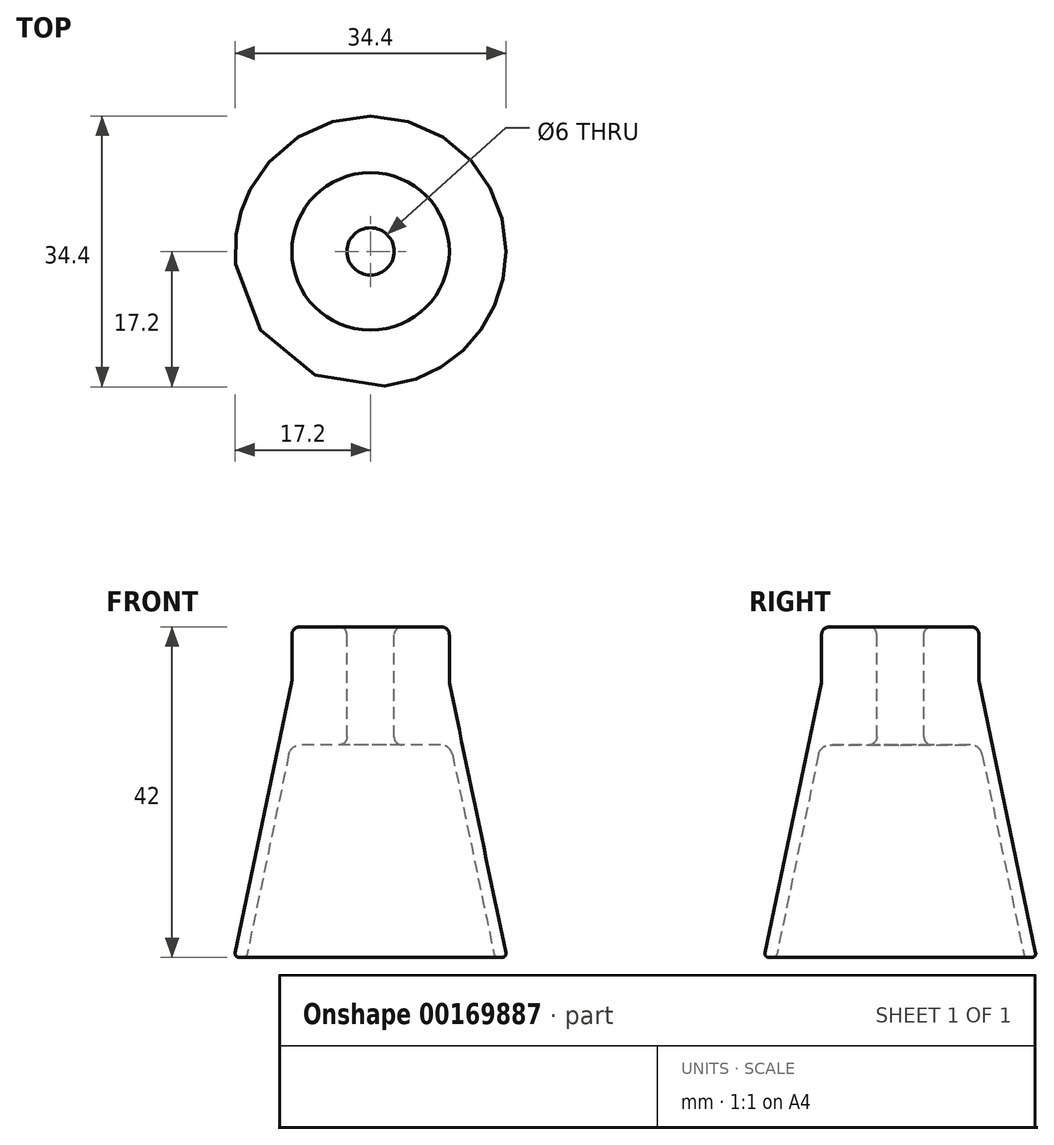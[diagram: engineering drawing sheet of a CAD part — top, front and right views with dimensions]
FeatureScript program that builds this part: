
annotation { "Feature Type Name" : "Feature", "Feature Type Description" : "" }
export const myFeature = defineFeature(function(context is Context, id is Id, definition is map)
    precondition{}
    {
        {
            var Q0;
            Q0=qCreatedBy(makeId("Right.planeOp"),FACE);
            var sketch = newSketch(context, id + "F0", { "sketchPlane" : qUnion([Q0])});
            skLineSegment(sketch, "E0", {"start": v(0, 42) * mm, "end": v(0, 0) * mm, "construction": true});
            skLineSegment(sketch, "E1", {"start": v(-4, 42) * mm, "end": v(-9, 42) * mm});
            skLineSegment(sketch, "E2", {"start": v(-10, 41) * mm, "end": v(-10, 35.16) * mm});
            skLineSegment(sketch, "E3", {"start": v(-10.03, 34.85) * mm, "end": v(-17.19, 0.6) * mm});
            skLineSegment(sketch, "E4", {"start": v(-16.7, 0) * mm, "end": v(-16.19, 0) * mm});
            skLineSegment(sketch, "E5", {"start": v(-15.7, 0.4) * mm, "end": v(-10.39, 25.8) * mm});
            skLineSegment(sketch, "E6", {"start": v(-8.92, 27) * mm, "end": v(-4, 27) * mm});
            skLineSegment(sketch, "E7", {"start": v(-3, 28) * mm, "end": v(-3, 41) * mm});
            skLineSegment(sketch, "E8", {"start": v(-10, 42) * mm, "end": v(0, 42) * mm, "construction": true});
            skLineSegment(sketch, "E9", {"start": v(0, 0) * mm, "end": v(-18, 0) * mm, "construction": true});
            skLineSegment(sketch, "E10", {"start": v(0, 35.16) * mm, "end": v(-3, 35.16) * mm, "construction": true});
            skPoint(sketch, "E11.visualSharp", {"position": v(-3, 27) * mm});
            skArc(sketch, "E11.filletArc", {"start": v(-4, 27) * mm, "mid": v(-3.3, 27.3) * mm, "end": v(-3, 28) * mm});
            skPoint(sketch, "E12.visualSharp", {"position": v(-3, 42) * mm});
            skArc(sketch, "E12.filletArc", {"start": v(-3, 41) * mm, "mid": v(-3.3, 41.7) * mm, "end": v(-4, 42) * mm});
            skPoint(sketch, "E13.visualSharp", {"position": v(-10, 42) * mm});
            skArc(sketch, "E13.filletArc", {"start": v(-9, 42) * mm, "mid": v(-9.7, 41.7) * mm, "end": v(-10, 41) * mm});
            skPoint(sketch, "E14.visualSharp", {"position": v(-17.31, 0) * mm});
            skArc(sketch, "E14.filletArc", {"start": v(-17.19, 0.6) * mm, "mid": v(-17.08, 0.18) * mm, "end": v(-16.7, 0) * mm});
            skPoint(sketch, "E15.visualSharp", {"position": v(-15.78, 0) * mm});
            skArc(sketch, "E15.filletArc", {"start": v(-16.19, 0) * mm, "mid": v(-15.87, 0.11) * mm, "end": v(-15.7, 0.4) * mm});
            skPoint(sketch, "E16.visualSharp", {"position": v(-10.14, 27) * mm});
            skArc(sketch, "E16.filletArc", {"start": v(-8.92, 27) * mm, "mid": v(-9.87, 26.66) * mm, "end": v(-10.39, 25.8) * mm});
            skPoint(sketch, "E17.visualSharp", {"position": v(-10, 35) * mm});
            skArc(sketch, "E17.filletArc", {"start": v(-10.03, 34.85) * mm, "mid": v(-10, 35) * mm, "end": v(-10, 35.16) * mm});
            skSolve(sketch);
        }
        {
            var Q0;
            Q0=makeQuery(id+"F0.imprint","IMPRINT",FACE,{"disambiguationData":[TD([[makeQuery(id+"F0.imprint","IMPRINT",EDGE,{"derivedFrom":sQuery(id+"F0.wireOp",EDGE,"E1")}),1.0]])]});
            var Q1;
            Q1=sQuery(id+"F0.wireOp",EDGE,"E0");
            revolve(context, id + "F1", {"entities" : qUnion([Q0]), "axis" : qUnion([Q1]), "revolveType" : RevolveType.FULL});
        }
    });
